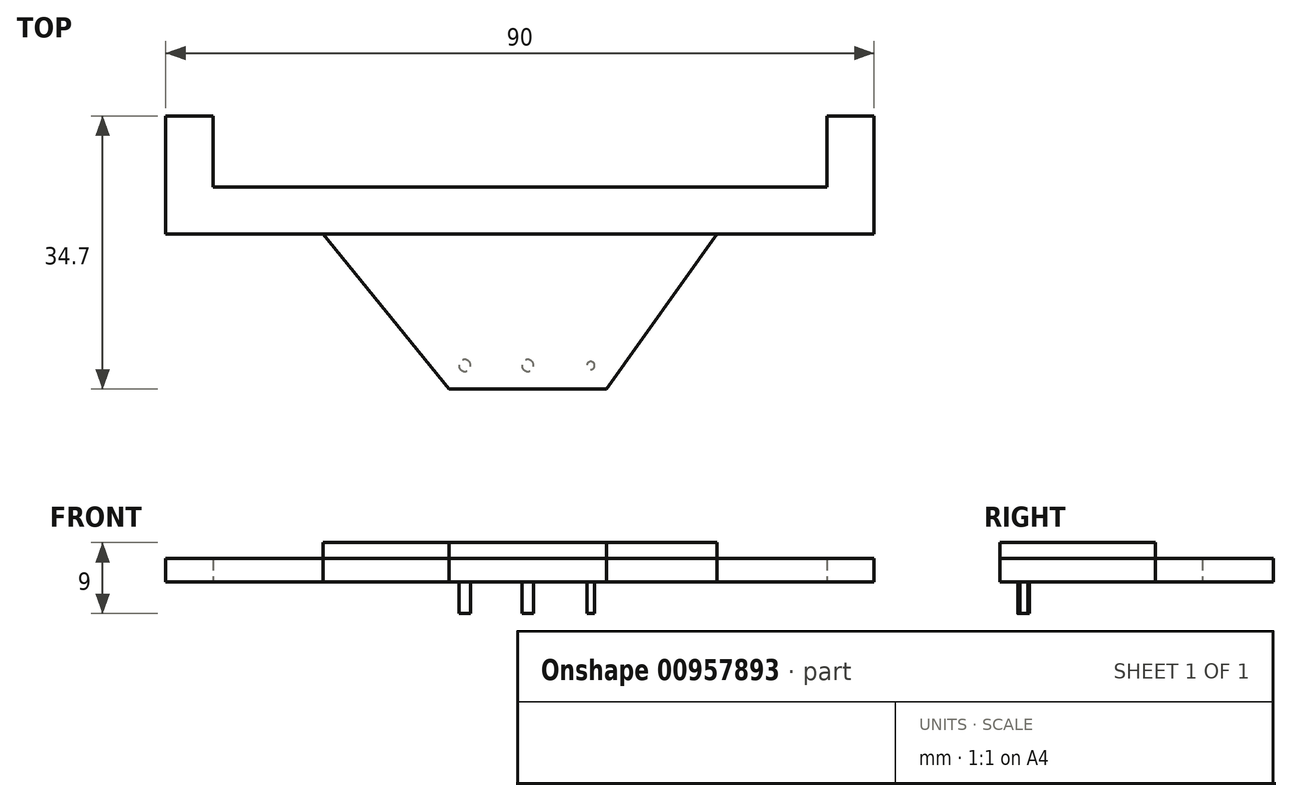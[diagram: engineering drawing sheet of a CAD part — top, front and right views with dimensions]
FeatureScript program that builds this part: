
annotation { "Feature Type Name" : "Feature", "Feature Type Description" : "" }
export const myFeature = defineFeature(function(context is Context, id is Id, definition is map)
    precondition{}
    {
        {
            var Q0;
            Q0=qCreatedBy(makeId("Top.planeOp"),FACE);
            var sketch = newSketch(context, id + "F0", { "sketchPlane" : qUnion([Q0])});
            skLineSegment(sketch, "E0", {"start": v(-46, 0) * mm, "end": v(-46, 15) * mm});
            skLineSegment(sketch, "E1", {"start": v(-46, 15) * mm, "end": v(-40, 15) * mm});
            skLineSegment(sketch, "E2", {"start": v(-40, 15) * mm, "end": v(-40, 6) * mm});
            skLineSegment(sketch, "E3", {"start": v(-40, 6) * mm, "end": v(38, 6) * mm});
            skLineSegment(sketch, "E4", {"start": v(38, 6) * mm, "end": v(38, 15) * mm});
            skLineSegment(sketch, "E5", {"start": v(38, 15) * mm, "end": v(44, 15) * mm});
            skLineSegment(sketch, "E6", {"start": v(44, 15) * mm, "end": v(44, 0) * mm});
            skLineSegment(sketch, "E7", {"start": v(-46, 0) * mm, "end": v(44, 0) * mm});
            skPoint(sketch, "E8", {"position": v(-26, 0) * mm});
            skPoint(sketch, "E9", {"position": v(24, 0) * mm});
            skPoint(sketch, "E10", {"position": v(0, -19.7) * mm});
            skPoint(sketch, "E11", {"position": v(-10, -19.7) * mm});
            skPoint(sketch, "E12", {"position": v(10, -19.7) * mm});
            skLineSegment(sketch, "E13", {"start": v(-26, 0) * mm, "end": v(-10, -19.7) * mm});
            skLineSegment(sketch, "E14", {"start": v(10, -19.7) * mm, "end": v(-10, -19.7) * mm});
            skLineSegment(sketch, "E15", {"start": v(10, -19.7) * mm, "end": v(24, 0) * mm});
            skSolve(sketch);
        }
        {
            var Q0;
            Q0 = qSketchRegion(id + "F0", true);
            extrude(context, id + "F1", {"entities" : qUnion([Q0]), "depth" : 3 * mm, "offsetDistance" : 25 * mm});
        }
        {
            var Q0;
            Q0=makeQuery(id+"F1.opExtrude","CAP_FACE",FACE,{"disambiguationData":[OSD([sQuery(id+"F0.wireOp",EDGE,"E0"),sQuery(id+"F0.wireOp",EDGE,"E1"),sQuery(id+"F0.wireOp",EDGE,"E2"),sQuery(id+"F0.wireOp",EDGE,"E3"),sQuery(id+"F0.wireOp",EDGE,"E4"),sQuery(id+"F0.wireOp",EDGE,"E5"),sQuery(id+"F0.wireOp",EDGE,"E6"),sQuery(id+"F0.wireOp",EDGE,"E7"),sQuery(id+"F0.wireOp",EDGE,"E13"),sQuery(id+"F0.wireOp",EDGE,"E14"),sQuery(id+"F0.wireOp",EDGE,"E15")])],"isStart":false});
            var sketch = newSketch(context, id + "F2", { "sketchPlane" : qUnion([Q0])});
            skLineSegment(sketch, "E16", {"start": v(-26, 0) * mm, "end": v(24, 0) * mm});
            skLineSegment(sketch, "E17", {"start": v(24, 0) * mm, "end": v(10, -19.7) * mm});
            skLineSegment(sketch, "E18", {"start": v(10, -19.7) * mm, "end": v(-10, -19.7) * mm});
            skLineSegment(sketch, "E19", {"start": v(-10, -19.7) * mm, "end": v(-26, 0) * mm});
            skSolve(sketch);
        }
        {
            var Q0;
            Q0=makeQuery(id+"F2.imprint","IMPRINT",FACE,{"disambiguationData":[TD([[makeQuery(id+"F2.imprint","IMPRINT",EDGE,{"derivedFrom":sQuery(id+"F2.wireOp",EDGE,"E16")}),-1.0]])]});
            extrude(context, id + "F3", {"entities" : qUnion([Q0]), "depth" : 2 * mm, "offsetDistance" : 25 * mm});
        }
        {
            var Q0;
            Q0=makeQuery(id+"F1.opExtrude","CAP_FACE",FACE,{"disambiguationData":[OSD([sQuery(id+"F0.wireOp",EDGE,"E0"),sQuery(id+"F0.wireOp",EDGE,"E1"),sQuery(id+"F0.wireOp",EDGE,"E2"),sQuery(id+"F0.wireOp",EDGE,"E3"),sQuery(id+"F0.wireOp",EDGE,"E4"),sQuery(id+"F0.wireOp",EDGE,"E5"),sQuery(id+"F0.wireOp",EDGE,"E6"),sQuery(id+"F0.wireOp",EDGE,"E7"),sQuery(id+"F0.wireOp",EDGE,"E13"),sQuery(id+"F0.wireOp",EDGE,"E14"),sQuery(id+"F0.wireOp",EDGE,"E15")])],"isStart":true});
            var sketch = newSketch(context, id + "F4", { "sketchPlane" : qUnion([Q0])});
            skPoint(sketch, "E20", {"position": v(0, 16.7) * mm});
            skPoint(sketch, "E21", {"position": v(-8, 16.7) * mm});
            skPoint(sketch, "E22", {"position": v(8, 16.7) * mm});
            skCircle(sketch, "E23", {"center": v(-8, 16.7) * mm, "radius": 0.75 * mm});
            skCircle(sketch, "E24", {"center": v(0, 16.7) * mm, "radius": 0.75 * mm});
            skCircle(sketch, "E25", {"center": v(8, 16.7) * mm, "radius": 0.5 * mm});
            skSolve(sketch);
        }
        {
            var Q0;
            Q0=makeQuery(id+"F4.imprint","IMPRINT",FACE,{"disambiguationData":[TD([[makeQuery(id+"F4.imprint","IMPRINT",EDGE,{"derivedFrom":sQuery(id+"F4.wireOp",EDGE,"E24")}),1.0]])]});
            var Q1;
            Q1=makeQuery(id+"F4.imprint","IMPRINT",FACE,{"disambiguationData":[TD([[makeQuery(id+"F4.imprint","IMPRINT",EDGE,{"derivedFrom":sQuery(id+"F4.wireOp",EDGE,"E25")}),1.0]])]});
            var Q2;
            Q2=makeQuery(id+"F4.imprint","IMPRINT",FACE,{"disambiguationData":[TD([[makeQuery(id+"F4.imprint","IMPRINT",EDGE,{"derivedFrom":sQuery(id+"F4.wireOp",EDGE,"E23")}),1.0]])]});
            extrude(context, id + "F5", {"entities" : qUnion([Q0, Q1, Q2]), "depth" : 4 * mm, "offsetDistance" : 25 * mm});
        }
    });
